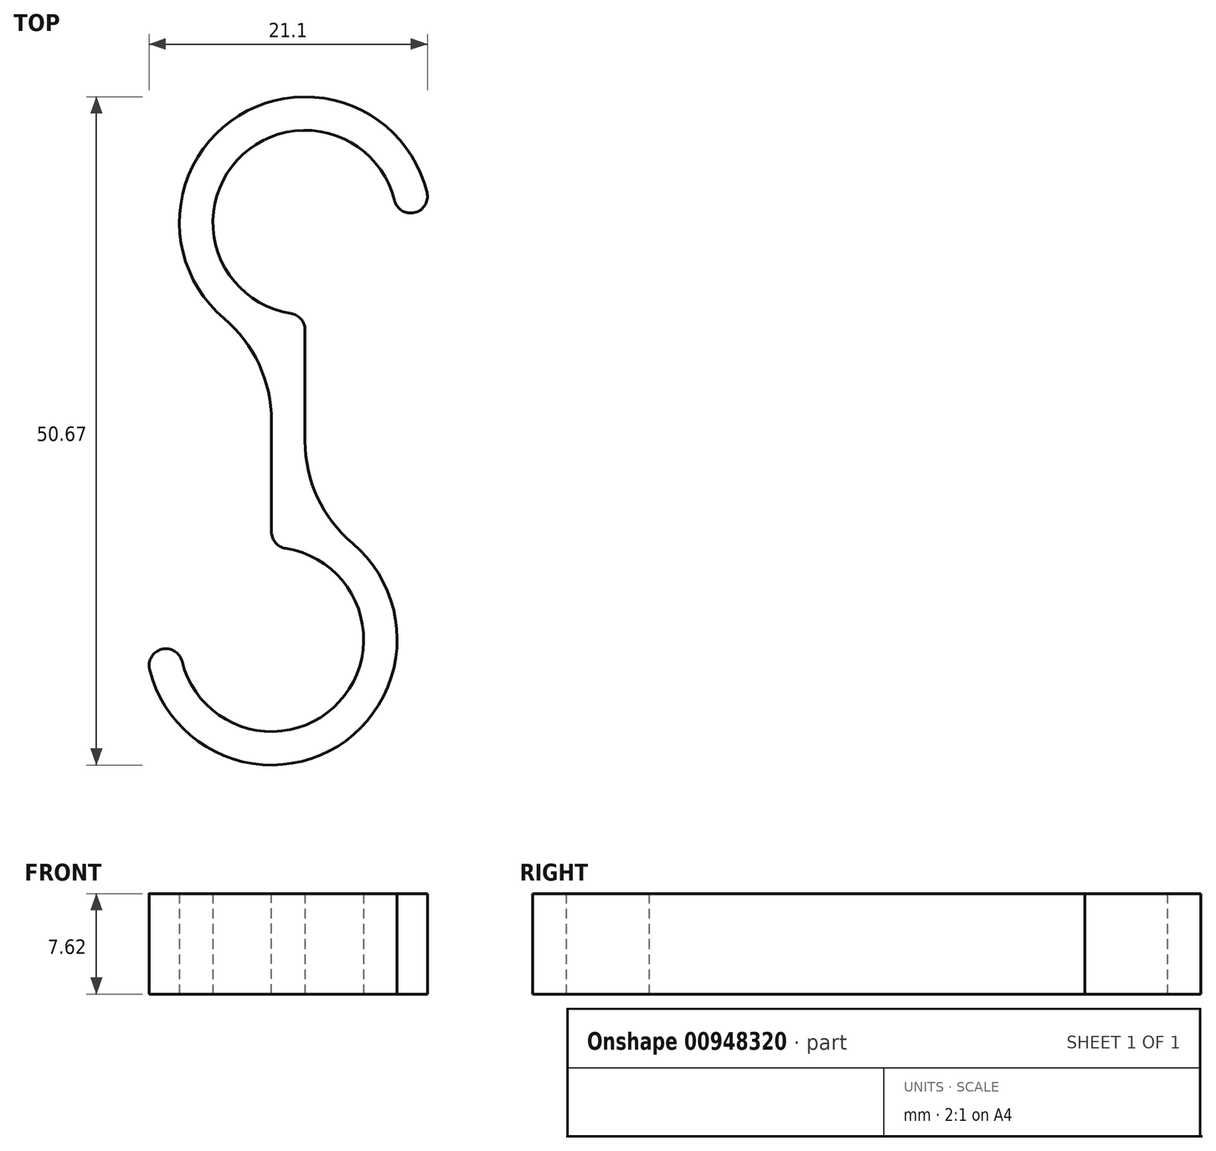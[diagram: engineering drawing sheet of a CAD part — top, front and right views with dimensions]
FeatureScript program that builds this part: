
annotation { "Feature Type Name" : "Feature", "Feature Type Description" : "" }
export const myFeature = defineFeature(function(context is Context, id is Id, definition is map)
    precondition{}
    {
        {
            var Q0;
            Q0=qCreatedBy(makeId("Top.planeOp"),FACE);
            var sketch = newSketch(context, id + "F0", { "sketchPlane" : qUnion([Q0])});
            skArc(sketch, "E0", {"start": v(6.96, 0.6) * mm, "mid": v(-5.15, 4.72) * mm, "end": v(0, -6.99) * mm});
            skArc(sketch, "E1", {"start": v(9.49, 0.83) * mm, "mid": v(-6.1, 7.32) * mm, "end": v(-2.54, -9.18) * mm});
            skLineSegment(sketch, "E2", {"start": v(0, -6.99) * mm, "end": v(0, -9.53) * mm});
            skLineSegment(sketch, "E3", {"start": v(6.96, 0.6) * mm, "end": v(9.49, 0.83) * mm});
            skArc(sketch, "E4", {"start": v(-9.5, -32.23) * mm, "mid": v(2.6, -36.34) * mm, "end": v(-2.54, -24.63) * mm});
            skArc(sketch, "E5", {"start": v(-12.03, -32.45) * mm, "mid": v(3.55, -38.94) * mm, "end": v(0, -22.44) * mm});
            skLineSegment(sketch, "E6", {"start": v(-2.54, -22.1) * mm, "end": v(-2.54, -24.63) * mm});
            skLineSegment(sketch, "E7", {"start": v(-9.5, -32.23) * mm, "end": v(-12.03, -32.45) * mm});
            skLineSegment(sketch, "E8", {"start": v(0, -9.53) * mm, "end": v(0, -22.44) * mm});
            skLineSegment(sketch, "E9", {"start": v(-2.54, -9.18) * mm, "end": v(-2.54, -22.1) * mm});
            skSolve(sketch);
        }
        {
            var Q0;
            Q0=makeQuery(id+"F0.imprint","IMPRINT",FACE,{"disambiguationData":[TD([[makeQuery(id+"F0.imprint","IMPRINT",EDGE,{"derivedFrom":sQuery(id+"F0.wireOp",EDGE,"E0")}),-1.0]])]});
            extrude(context, id + "F1", {"entities" : qUnion([Q0]), "depth" : 7.62 * mm, "offsetDistance" : 25.4 * mm});
        }
        {
            var Q0;
            Q0=makeQuery(id+"F1.opExtrude","SWEPT_EDGE",EDGE,{"disambiguationData":[OSD([sQuery(id+"F0.wireOp",EDGE,"E1"),sQuery(id+"F0.wireOp",EDGE,"E9")])]});
            var Q1;
            Q1=makeQuery(id+"F1.opExtrude","SWEPT_EDGE",EDGE,{"disambiguationData":[OSD([sQuery(id+"F0.wireOp",EDGE,"E5"),sQuery(id+"F0.wireOp",EDGE,"E8")])]});
            fillet(context, id + "F2", {"entities" : qUnion([Q0, Q1]), "radius" : 10.16 * mm, "tangentPropagation" : true, "allowEdgeOverflow" : false});
        }
        {
            var Q0;
            Q0=makeQuery(id+"F1.opExtrude","SWEPT_EDGE",EDGE,{"disambiguationData":[OSD([sQuery(id+"F0.wireOp",EDGE,"E0"),sQuery(id+"F0.wireOp",EDGE,"E3")])]});
            var Q1;
            Q1=makeQuery(id+"F1.opExtrude","SWEPT_EDGE",EDGE,{"disambiguationData":[OSD([sQuery(id+"F0.wireOp",EDGE,"E1"),sQuery(id+"F0.wireOp",EDGE,"E3")])]});
            var Q2;
            Q2=makeQuery(id+"F1.opExtrude","SWEPT_EDGE",EDGE,{"disambiguationData":[OSD([sQuery(id+"F0.wireOp",EDGE,"E5"),sQuery(id+"F0.wireOp",EDGE,"E7")])]});
            var Q3;
            Q3=makeQuery(id+"F1.opExtrude","SWEPT_EDGE",EDGE,{"disambiguationData":[OSD([sQuery(id+"F0.wireOp",EDGE,"E4"),sQuery(id+"F0.wireOp",EDGE,"E7")])]});
            var Q4;
            Q4=makeQuery(id+"F1.opExtrude","SWEPT_EDGE",EDGE,{"disambiguationData":[OSD([sQuery(id+"F0.wireOp",EDGE,"E4"),sQuery(id+"F0.wireOp",EDGE,"E6")])]});
            var Q5;
            Q5=makeQuery(id+"F1.opExtrude","SWEPT_EDGE",EDGE,{"disambiguationData":[OSD([sQuery(id+"F0.wireOp",EDGE,"E0"),sQuery(id+"F0.wireOp",EDGE,"E2")])]});
            fillet(context, id + "F3", {"entities" : qUnion([Q0, Q1, Q2, Q3, Q4, Q5]), "radius" : 1.27 * mm, "tangentPropagation" : true, "allowEdgeOverflow" : false});
        }
    });
